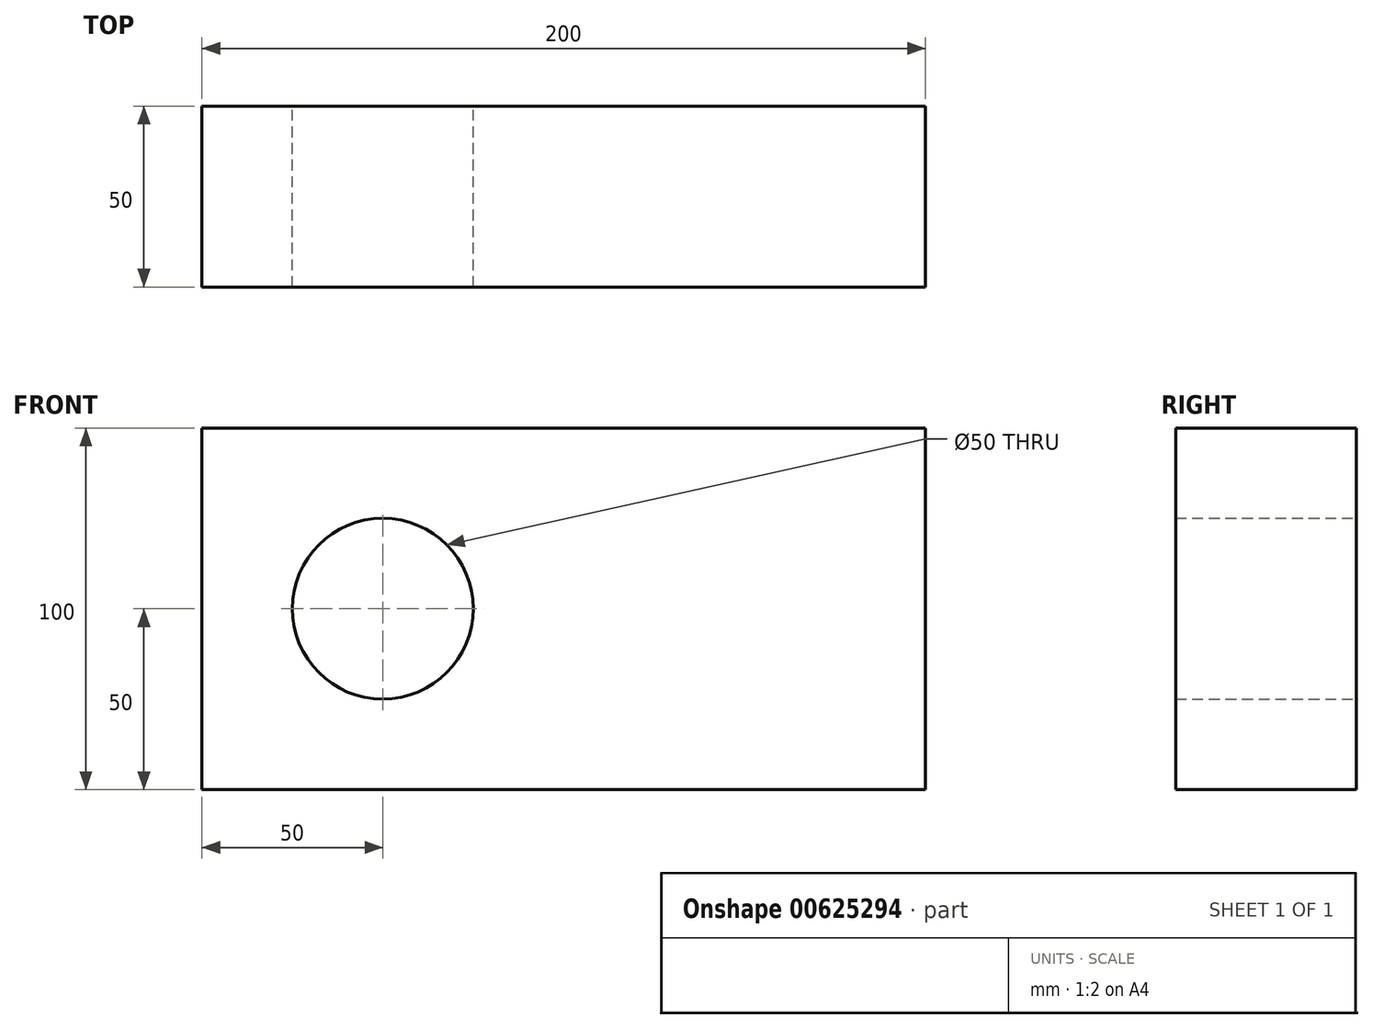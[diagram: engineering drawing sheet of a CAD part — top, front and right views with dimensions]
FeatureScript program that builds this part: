
annotation { "Feature Type Name" : "Feature", "Feature Type Description" : "" }
export const myFeature = defineFeature(function(context is Context, id is Id, definition is map)
    precondition{}
    {
        {
            var Q0;
            Q0=qCreatedBy(makeId("Front.planeOp"),FACE);
            var sketch = newSketch(context, id + "F0", { "sketchPlane" : qUnion([Q0])});
            skLineSegment(sketch, "E0.bottom", {"start": v(0, 0) * mm, "end": v(-200, 0) * mm});
            skLineSegment(sketch, "E0.top", {"start": v(0, 100) * mm, "end": v(-100, 100) * mm});
            skLineSegment(sketch, "E0.left", {"start": v(0, 0) * mm, "end": v(0, 100) * mm});
            skLineSegment(sketch, "E0.right", {"start": v(-200, 0) * mm, "end": v(-200, 100) * mm});
            skLineSegment(sketch, "E1", {"start": v(-100, 100) * mm, "end": v(-100, 0) * mm});
            skLineSegment(sketch, "E2", {"start": v(-200, 100) * mm, "end": v(-100, 100) * mm});
            skCircle(sketch, "E3", {"center": v(-150, 50) * mm, "radius": 25 * mm});
            skPoint(sketch, "E3.centerSnap0", {"position": v(-200, 50) * mm});
            skPoint(sketch, "E3.centerSnap1", {"position": v(-150, 100) * mm});
            skSolve(sketch);
        }
        {
            var Q0;
            Q0 = qSketchRegion(id + "F0", true);
            extrude(context, id + "F1", {"entities" : qUnion([Q0]), "depth" : 50 * mm, "offsetDistance" : 25 * mm});
        }
    });
